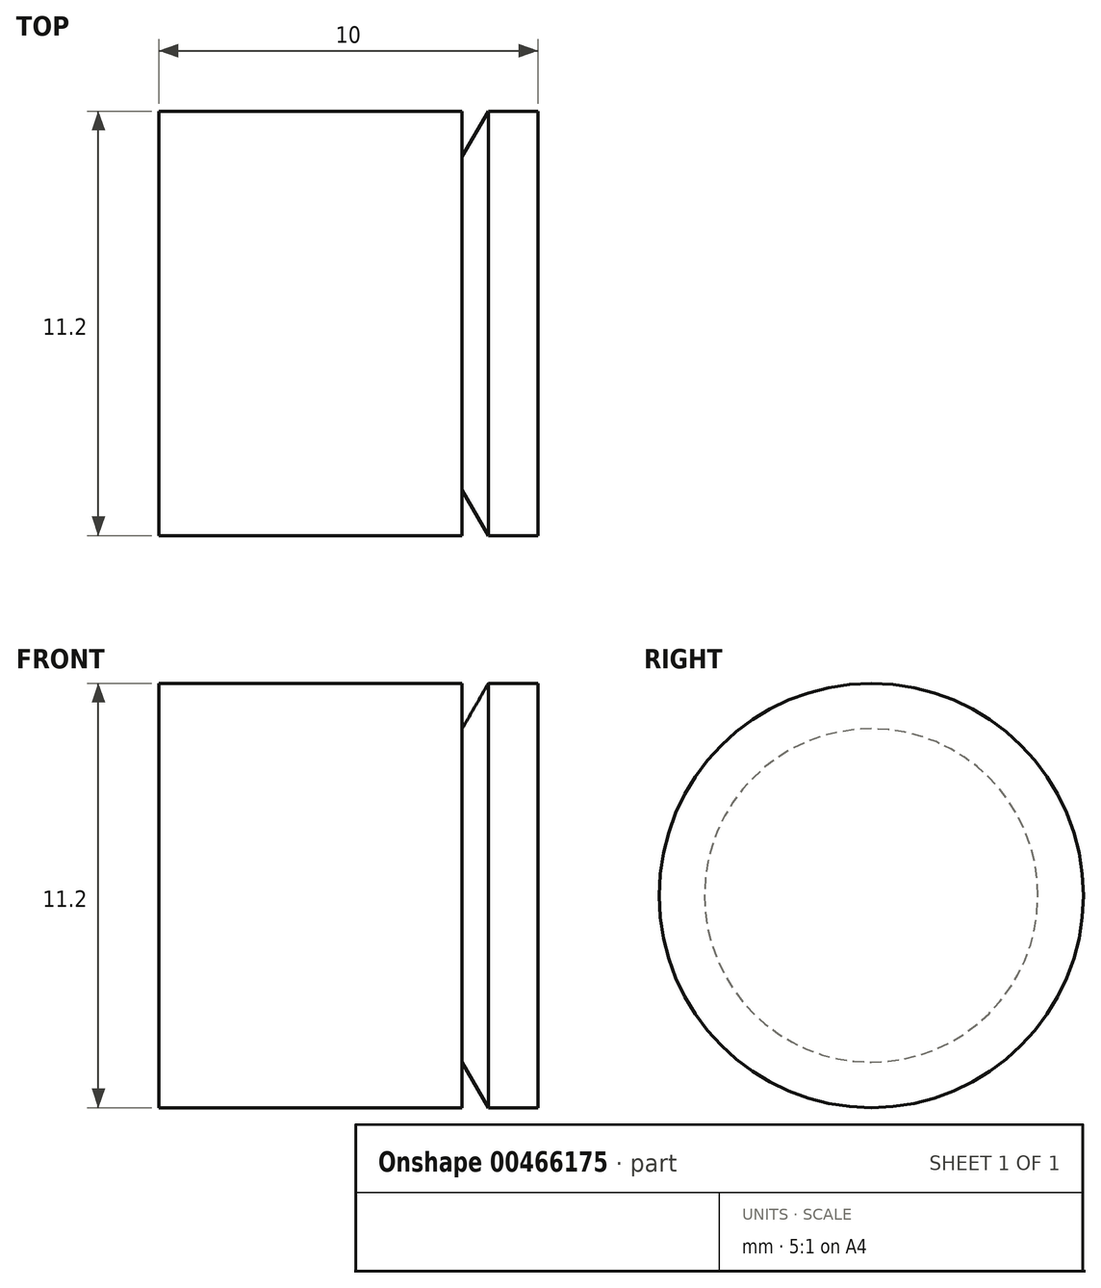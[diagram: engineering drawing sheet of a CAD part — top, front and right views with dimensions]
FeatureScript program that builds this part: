
annotation { "Feature Type Name" : "Feature", "Feature Type Description" : "" }
export const myFeature = defineFeature(function(context is Context, id is Id, definition is map)
    precondition{}
    {
        {
            var Q0;
            Q0=qCreatedBy(makeId("Front.planeOp"),FACE);
            var sketch = newSketch(context, id + "F0", { "sketchPlane" : qUnion([Q0])});
            skLineSegment(sketch, "E0", {"start": v(0, 0) * mm, "end": v(10, 0) * mm});
            skLineSegment(sketch, "E1", {"start": v(10, 0) * mm, "end": v(10, 5.6) * mm});
            skLineSegment(sketch, "E2", {"start": v(10, 5.6) * mm, "end": v(8.7, 5.6) * mm});
            skLineSegment(sketch, "E3", {"start": v(8.7, 5.6) * mm, "end": v(8, 4.4) * mm});
            skLineSegment(sketch, "E4", {"start": v(8, 4.4) * mm, "end": v(8, 5.6) * mm});
            skLineSegment(sketch, "E5", {"start": v(8, 5.6) * mm, "end": v(0, 5.6) * mm});
            skLineSegment(sketch, "E6", {"start": v(0, 5.6) * mm, "end": v(0, 0) * mm});
            skSolve(sketch);
        }
        {
            var Q0;
            Q0=makeQuery(id+"F0.imprint","IMPRINT",FACE,{"disambiguationData":[TD([[makeQuery(id+"F0.imprint","IMPRINT",EDGE,{"derivedFrom":sQuery(id+"F0.wireOp",EDGE,"E0")}),1.0]])]});
            var Q1;
            Q1=sQuery(id+"F0.wireOp",EDGE,"E0");
            revolve(context, id + "F1", {"entities" : qUnion([Q0]), "axis" : qUnion([Q1]), "revolveType" : RevolveType.FULL});
        }
    });
